# Revit family: TROSTEN FCU-Single Skin
name_source: partatom
category: Mechanical Equipment
units: mm (PartAtom-declared; Revit-internal decimal feet)

## family parameters
Always vertical = Yes
Cut with Voids When Loaded = No
OmniClass Number = 23.75.00.00
OmniClass Title = Climate Control (HVAC)
Part Type = Normal
Room Calculation Point = No
Round Connector Dimension = Use Radius
Shared = No
Work Plane-Based = No

## types (3) — shared parameters
Radius Drain = 10 mm  [stored 0.0328084 ft]
Radius Return = 10 mm  [stored 0.0328084 ft]
Radius Supply = 10 mm  [stored 0.0328084 ft]
Supply Mouth Depth = 20 mm  [stored 0.0656168 ft]
Type Comments = FCU-528
zero-valued in all types: Default Elevation

## per-type parameters (varying)
| type | FCU Overall Depth | FCU Overall Height | FCU Overall Width | Return Mouth Height | Return Mouth Width | Supply Mouth Height | Supply Mouth Width |
| TFC M-035 4D CS A5G | 577 mm  [stored 1.89304 ft] | 250 mm  [stored 0.82021 ft] | 822 mm  [stored 2.69685 ft] | 200 mm  [stored 0.656168 ft] | 802 mm  [stored 2.63123 ft] | 200 mm  [stored 0.656168 ft] | 802 mm  [stored 2.63123 ft] |
| TFC M-045 4D CS A5G | 577 mm  [stored 1.89304 ft] | 250 mm  [stored 0.82021 ft] | 822 mm  [stored 2.69685 ft] | 200 mm  [stored 0.656168 ft] | 802 mm  [stored 2.63123 ft] | 200 mm  [stored 0.656168 ft] | 802 mm  [stored 2.63123 ft] |
| TFC M-075 4D CS A5G | 637 mm  [stored 2.0899 ft] | 358 mm  [stored 1.17454 ft] | 927 mm  [stored 3.04134 ft] | 308 mm  [stored 1.0105 ft] | 907 mm  [stored 2.97572 ft] | 308 mm  [stored 1.0105 ft] | 907 mm  [stored 2.97572 ft] |

note: [stored X ft] marks values corroborated as IEEE doubles in the binary element streams (Revit-internal decimal feet)

## geometry (parser evidence)
native form markers: Sweep x4
no freeform markers — native parametric forms only
